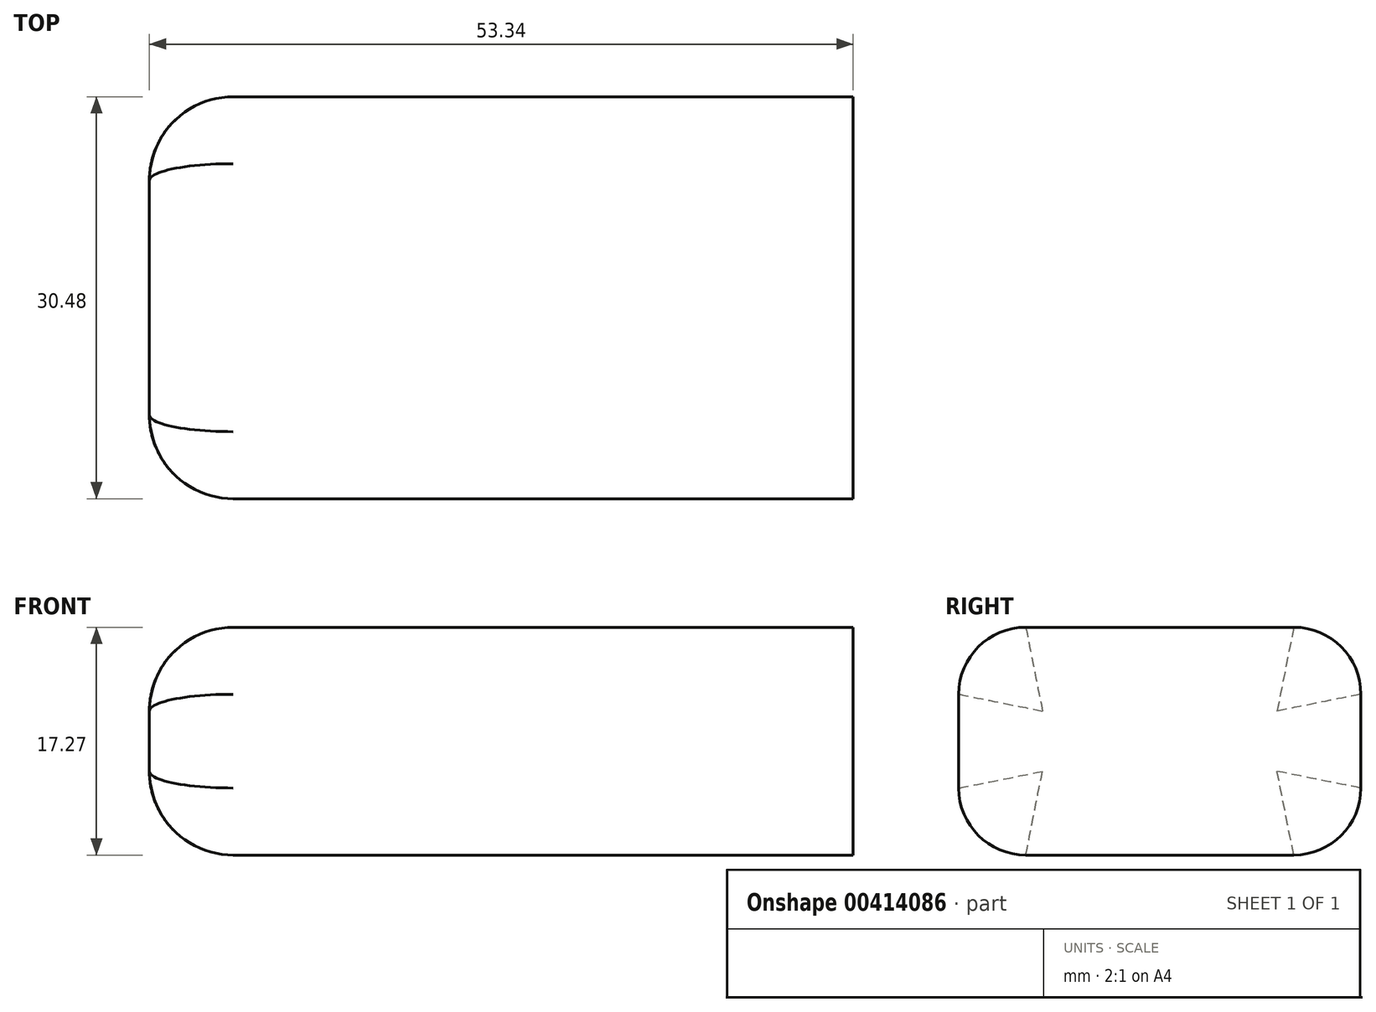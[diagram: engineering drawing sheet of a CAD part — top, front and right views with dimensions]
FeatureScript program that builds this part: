
annotation { "Feature Type Name" : "Feature", "Feature Type Description" : "" }
export const myFeature = defineFeature(function(context is Context, id is Id, definition is map)
    precondition{}
    {
        {
            var Q0;
            Q0=qCreatedBy(makeId("Top.planeOp"),FACE);
            var sketch = newSketch(context, id + "F0", { "sketchPlane" : qUnion([Q0])});
            skLineSegment(sketch, "E0.bottom", {"start": v(1.77, 0) * mm, "end": v(55.1, 0) * mm});
            skLineSegment(sketch, "E0.top", {"start": v(1.77, 30.48) * mm, "end": v(55.1, 30.48) * mm});
            skLineSegment(sketch, "E0.left", {"start": v(1.77, 0) * mm, "end": v(1.77, 30.48) * mm});
            skLineSegment(sketch, "E0.right", {"start": v(55.1, 0) * mm, "end": v(55.1, 30.48) * mm});
            skSolve(sketch);
        }
        {
            var Q0;
            Q0=makeQuery(id+"F0.imprint","IMPRINT",FACE,{"disambiguationData":[TD([[makeQuery(id+"F0.imprint","IMPRINT",EDGE,{"derivedFrom":sQuery(id+"F0.wireOp",EDGE,"E0.bottom")}),1.0]])]});
            extrude(context, id + "F1", {"entities" : qUnion([Q0]), "depth" : 17.27 * mm});
        }
        {
            var Q0;
            Q0=makeQuery(id+"F1.opExtrude","CAP_EDGE",EDGE,{"disambiguationData":[OSD([sQuery(id+"F0.wireOp",EDGE,"E0.top")])],"isStart":false});
            var Q1;
            Q1=makeQuery(id+"F1.opExtrude","CAP_EDGE",EDGE,{"disambiguationData":[OSD([sQuery(id+"F0.wireOp",EDGE,"E0.top")])],"isStart":true});
            var Q2;
            Q2=makeQuery(id+"F1.opExtrude","CAP_EDGE",EDGE,{"disambiguationData":[OSD([sQuery(id+"F0.wireOp",EDGE,"E0.bottom")])],"isStart":true});
            var Q3;
            Q3=makeQuery(id+"F1.opExtrude","CAP_EDGE",EDGE,{"disambiguationData":[OSD([sQuery(id+"F0.wireOp",EDGE,"E0.bottom")])],"isStart":false});
            fillet(context, id + "F2", {"entities" : qUnion([Q0, Q1, Q2, Q3]), "radius" : 5.08 * mm, "tangentPropagation" : true, "allowEdgeOverflow" : false});
        }
        {
            var Q0;
            Q0=makeQuery(id+"F1.opExtrude","CAP_EDGE",EDGE,{"disambiguationData":[OSD([sQuery(id+"F0.wireOp",EDGE,"E0.left")])],"isStart":false});
            var Q1;
            Q1=makeQuery(id+"F2.opFillet","BLEND_EDGE",EDGE,{"blendedFrom":[makeQuery(id+"F1.opExtrude","CAP_EDGE",EDGE,{"disambiguationData":[OSD([sQuery(id+"F0.wireOp",EDGE,"E0.top")])],"isStart":false}),makeQuery(id+"F1.opExtrude","SWEPT_FACE",FACE,{"disambiguationData":[OSD([sQuery(id+"F0.wireOp",EDGE,"E0.left")])]})],"blendedInto":[makeQuery(id+"F1.opExtrude","SWEPT_FACE",FACE,{"disambiguationData":[OSD([sQuery(id+"F0.wireOp",EDGE,"E0.left")])]})]});
            var Q2;
            Q2=makeQuery(id+"F2.opFillet","BLEND_EDGE",EDGE,{"blendedFrom":[makeQuery(id+"F1.opExtrude","CAP_EDGE",EDGE,{"disambiguationData":[OSD([sQuery(id+"F0.wireOp",EDGE,"E0.bottom")])],"isStart":false}),makeQuery(id+"F1.opExtrude","SWEPT_FACE",FACE,{"disambiguationData":[OSD([sQuery(id+"F0.wireOp",EDGE,"E0.left")])]})],"blendedInto":[makeQuery(id+"F1.opExtrude","SWEPT_FACE",FACE,{"disambiguationData":[OSD([sQuery(id+"F0.wireOp",EDGE,"E0.left")])]})]});
            var Q3;
            Q3=makeQuery(id+"F2.opFillet","BLEND_EDGE",EDGE,{"blendedFrom":[makeQuery(id+"F1.opExtrude","CAP_EDGE",EDGE,{"disambiguationData":[OSD([sQuery(id+"F0.wireOp",EDGE,"E0.top")])],"isStart":true}),makeQuery(id+"F1.opExtrude","SWEPT_FACE",FACE,{"disambiguationData":[OSD([sQuery(id+"F0.wireOp",EDGE,"E0.left")])]})],"blendedInto":[makeQuery(id+"F1.opExtrude","SWEPT_FACE",FACE,{"disambiguationData":[OSD([sQuery(id+"F0.wireOp",EDGE,"E0.left")])]})]});
            var Q4;
            Q4=makeQuery(id+"F1.opExtrude","CAP_EDGE",EDGE,{"disambiguationData":[OSD([sQuery(id+"F0.wireOp",EDGE,"E0.left")])],"isStart":true});
            var Q5;
            Q5=makeQuery(id+"F2.opFillet","BLEND_EDGE",EDGE,{"blendedFrom":[makeQuery(id+"F1.opExtrude","CAP_EDGE",EDGE,{"disambiguationData":[OSD([sQuery(id+"F0.wireOp",EDGE,"E0.bottom")])],"isStart":true}),makeQuery(id+"F1.opExtrude","SWEPT_FACE",FACE,{"disambiguationData":[OSD([sQuery(id+"F0.wireOp",EDGE,"E0.left")])]})],"blendedInto":[makeQuery(id+"F1.opExtrude","SWEPT_FACE",FACE,{"disambiguationData":[OSD([sQuery(id+"F0.wireOp",EDGE,"E0.left")])]})]});
            fillet(context, id + "F3", {"entities" : qUnion([Q0, Q1, Q2, Q3, Q4, Q5]), "radius" : 6.35 * mm, "tangentPropagation" : true, "allowEdgeOverflow" : false});
        }
    });
